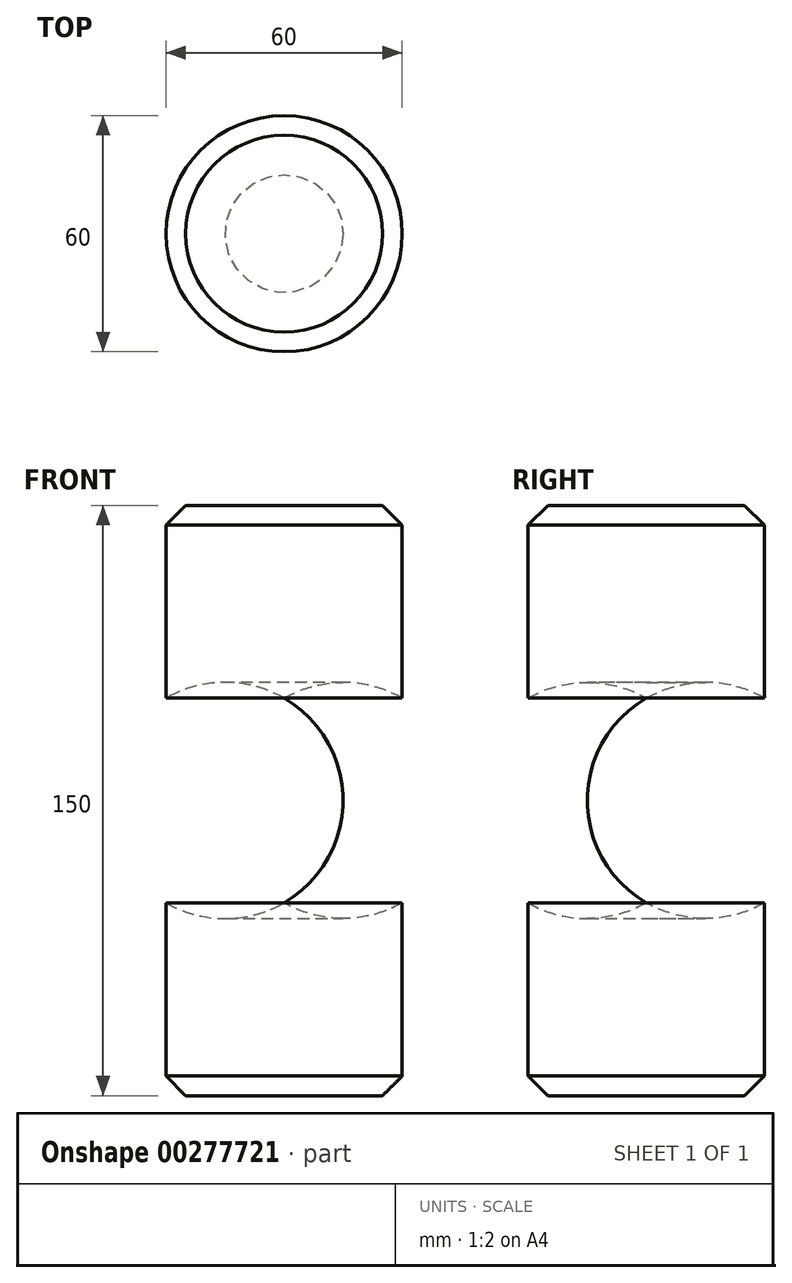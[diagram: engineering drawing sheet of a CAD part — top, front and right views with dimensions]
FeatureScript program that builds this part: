
annotation { "Feature Type Name" : "Feature", "Feature Type Description" : "" }
export const myFeature = defineFeature(function(context is Context, id is Id, definition is map)
    precondition{}
    {
        {
            var Q0;
            Q0=qCreatedBy(makeId("Front.planeOp"),FACE);
            var sketch = newSketch(context, id + "F0", { "sketchPlane" : qUnion([Q0])});
            skLineSegment(sketch, "E0", {"start": v(0, 75) * mm, "end": v(30, 75) * mm});
            skLineSegment(sketch, "E1", {"start": v(30, 75) * mm, "end": v(30, 25.98) * mm});
            skArc(sketch, "E2", {"start": v(30, -25.98) * mm, "mid": v(45, 0) * mm, "end": v(30, 25.98) * mm});
            skLineSegment(sketch, "E3", {"start": v(30, -25.98) * mm, "end": v(30, -75) * mm});
            skLineSegment(sketch, "E4", {"start": v(30, -75) * mm, "end": v(0, -75) * mm});
            skLineSegment(sketch, "E5", {"start": v(0, -75) * mm, "end": v(0, 75) * mm});
            skSolve(sketch);
        }
        {
            var Q0;
            Q0=makeQuery(id+"F0.imprint","IMPRINT",FACE,{"disambiguationData":[TD([[makeQuery(id+"F0.imprint","IMPRINT",EDGE,{"derivedFrom":sQuery(id+"F0.wireOp",EDGE,"E0")}),-1.0]])]});
            var Q1;
            Q1=sQuery(id+"F0.wireOp",EDGE,"E5");
            revolve(context, id + "F1", {"entities" : qUnion([Q0]), "axis" : qUnion([Q1]), "revolveType" : RevolveType.FULL});
        }
        {
            var Q0;
            Q0=qCreatedBy(makeId("Right.planeOp"),FACE);
            cPlane(context, id + "F2", {"entities" : qUnion([Q0]), "cplaneType" : CPlaneType.OFFSET, "offset" : 30 * mm, "width" : 150 * mm, "height" : 150 * mm});
        }
        {
            var Q0;
            Q0=qCreatedBy(id+"F2.planeOp",FACE);
            var sketch = newSketch(context, id + "F3", { "sketchPlane" : qUnion([Q0])});
            skEllipse(sketch, "E6", {"center": v(0, 0) * mm, "majorRadius": 20 * mm, "minorRadius": 10 * mm, "majorAxis": v(0, 1)});
            skSolve(sketch);
        }
        {
            var Q0;
            Q0=qCreatedBy(makeId("Front.planeOp"),FACE);
            var sketch = newSketch(context, id + "F4", { "sketchPlane" : qUnion([Q0])});
            skFitSpline(sketch, "E7", {"points": [v(30.54, 0) * mm, v(121.7, 9.88) * mm, v(170.2, 75) * mm, v(260.02, 115.86) * mm], "startDerivative": vector(310.56, -24.64) * mm, "endDerivative": vector(294.86, 80.72) * mm});
            skSolve(sketch);
        }
        {
            var Q0;
            Q0 = qSketchRegion(id + "F3", true);
            var Q1;
            Q1 = qConstructionFilter(qBodyType(qCreatedBy(id + "F4" ,EDGE), BodyType.WIRE), ConstructionObject.NO);
            sweep(context, id + "F5", {"operationType" : NewBodyOperationType.ADD, "profiles" : qUnion([Q0]), "path" : qUnion([Q1])});
        }
        {
            var Q0;
            Q0=makeQuery(id+"F1.opRevolve","SWEPT_BODY",BODY,{"disambiguationData":[OSD([sQuery(id+"F0.wireOp",EDGE,"E0"),sQuery(id+"F0.wireOp",EDGE,"E1"),sQuery(id+"F0.wireOp",EDGE,"E2"),sQuery(id+"F0.wireOp",EDGE,"E3"),sQuery(id+"F0.wireOp",EDGE,"E4"),sQuery(id+"F0.wireOp",EDGE,"E5")])]});
            var Q1;
            Q1=makeQuery(id+"F1.opRevolve","SWEPT_FACE",FACE,{"disambiguationData":[OSD([sQuery(id+"F0.wireOp",EDGE,"E1")])]});
            circularPattern(context, id + "F6", {"entities" : qUnion([Q0]), "axis" : qUnion([Q1]), "angle" : 360 * degree, "instanceCount" : 5, "equalSpace" : true});
        }
        {
            var Q0;
            Q0=qCreatedBy(makeId("Front.planeOp"),FACE);
            var sketch = newSketch(context, id + "F7", { "sketchPlane" : qUnion([Q0])});
            skCircle(sketch, "E8", {"center": v(280, 120) * mm, "radius": 30 * mm});
            skSolve(sketch);
        }
        {
            var Q0;
            Q0=makeQuery(id+"F7.imprint","IMPRINT",FACE,{"disambiguationData":[TD([[makeQuery(id+"F7.imprint","IMPRINT",EDGE,{"derivedFrom":sQuery(id+"F7.wireOp",EDGE,"E8")}),1.0]])]});
            var Q1;
            Q1=makeQuery(id+"F1.opRevolve","SWEPT_FACE",FACE,{"disambiguationData":[OSD([sQuery(id+"F0.wireOp",EDGE,"E1")])]});
            revolve(context, id + "F8", {"operationType" : NewBodyOperationType.ADD, "entities" : qUnion([Q0]), "axis" : qUnion([Q1]), "revolveType" : RevolveType.FULL});
        }
        {
            var Q0;
            Q0=makeQuery(id+"F5.boolean.opBoolean","INTERSECT",EDGE,{"derivedFrom":[makeQuery(id+"F1.opRevolve","SWEPT_FACE",FACE,{"disambiguationData":[OSD([sQuery(id+"F0.wireOp",EDGE,"E2")])]}),makeQuery(id+"F5.opSweep","SWEPT_FACE",FACE,{"disambiguationData":[OSD([sQuery(id+"F3.wireOp",EDGE,"E6"),sQuery(id+"F4.wireOp",EDGE,"E7")])]})]});
            var Q1;
            {var subQ0=makeQuery(id+"F1.opRevolve","SWEPT_FACE",FACE,{"disambiguationData":[OSD([sQuery(id+"F0.wireOp",EDGE,"E2")])]});Q1=makeQuery(id+"F8.boolean.opBoolean","INTERSECT",EDGE,{"derivedFrom":[subQ0,makeQuery(id+"F6.opPattern","COPY",FACE,{"derivedFrom":subQ0,"instanceName":"1"}),makeQuery(id+"F6.opPattern","COPY",FACE,{"derivedFrom":subQ0,"instanceName":"2"}),makeQuery(id+"F6.opPattern","COPY",FACE,{"derivedFrom":subQ0,"instanceName":"3"})]});}
            var Q2;
            {var subQ0=makeQuery(id+"F1.opRevolve","SWEPT_FACE",FACE,{"disambiguationData":[OSD([sQuery(id+"F0.wireOp",EDGE,"E2")])]});Q2=makeQuery(id+"F8.boolean.opBoolean","INTERSECT",EDGE,{"derivedFrom":[subQ0,makeQuery(id+"F6.opPattern","COPY",FACE,{"derivedFrom":subQ0,"instanceName":"1"}),makeQuery(id+"F6.opPattern","COPY",FACE,{"derivedFrom":subQ0,"instanceName":"2"}),makeQuery(id+"F6.opPattern","COPY",FACE,{"derivedFrom":subQ0,"instanceName":"4"})]});}
            var Q3;
            {var subQ0=makeQuery(id+"F1.opRevolve","SWEPT_FACE",FACE,{"disambiguationData":[OSD([sQuery(id+"F0.wireOp",EDGE,"E2")])]});Q3=makeQuery(id+"F8.boolean.opBoolean","INTERSECT",EDGE,{"derivedFrom":[subQ0,makeQuery(id+"F6.opPattern","COPY",FACE,{"derivedFrom":subQ0,"instanceName":"1"}),makeQuery(id+"F6.opPattern","COPY",FACE,{"derivedFrom":subQ0,"instanceName":"3"})]});}
            var Q4;
            {var subQ0=makeQuery(id+"F1.opRevolve","SWEPT_FACE",FACE,{"disambiguationData":[OSD([sQuery(id+"F0.wireOp",EDGE,"E2")])]});Q4=makeQuery(id+"F8.boolean.opBoolean","INTERSECT",EDGE,{"derivedFrom":[subQ0,makeQuery(id+"F6.opPattern","COPY",FACE,{"derivedFrom":subQ0,"instanceName":"2"})]});}
            fillet(context, id + "F9", {"entities" : qUnion([Q0, Q1, Q2, Q3, Q4]), "radius" : 10 * mm, "tangentPropagation" : true, "allowEdgeOverflow" : false});
        }
        {
            var Q0;
            Q0=makeQuery(id+"F8.boolean.opBoolean","INTERSECT",EDGE,{"derivedFrom":[makeQuery(id+"F5.opSweep","SWEPT_FACE",FACE,{"disambiguationData":[OSD([sQuery(id+"F3.wireOp",EDGE,"E6"),sQuery(id+"F4.wireOp",EDGE,"E7")])]}),makeQuery(id+"F8.opRevolve","SWEPT_FACE",FACE,{"disambiguationData":[OSD([sQuery(id+"F7.wireOp",EDGE,"E8")])]})]});
            var Q1;
            Q1=makeQuery(id+"F8.boolean.opBoolean","INTERSECT",EDGE,{"derivedFrom":[makeQuery(id+"F6.opPattern","COPY",FACE,{"derivedFrom":makeQuery(id+"F5.opSweep","SWEPT_FACE",FACE,{"disambiguationData":[OSD([sQuery(id+"F3.wireOp",EDGE,"E6"),sQuery(id+"F4.wireOp",EDGE,"E7")])]}),"instanceName":"1"}),makeQuery(id+"F8.opRevolve","SWEPT_FACE",FACE,{"disambiguationData":[OSD([sQuery(id+"F7.wireOp",EDGE,"E8")])]})]});
            var Q2;
            Q2=makeQuery(id+"F8.boolean.opBoolean","INTERSECT",EDGE,{"derivedFrom":[makeQuery(id+"F6.opPattern","COPY",FACE,{"derivedFrom":makeQuery(id+"F5.opSweep","SWEPT_FACE",FACE,{"disambiguationData":[OSD([sQuery(id+"F3.wireOp",EDGE,"E6"),sQuery(id+"F4.wireOp",EDGE,"E7")])]}),"instanceName":"2"}),makeQuery(id+"F8.opRevolve","SWEPT_FACE",FACE,{"disambiguationData":[OSD([sQuery(id+"F7.wireOp",EDGE,"E8")])]})]});
            var Q3;
            Q3=makeQuery(id+"F8.boolean.opBoolean","INTERSECT",EDGE,{"derivedFrom":[makeQuery(id+"F6.opPattern","COPY",FACE,{"derivedFrom":makeQuery(id+"F5.opSweep","SWEPT_FACE",FACE,{"disambiguationData":[OSD([sQuery(id+"F3.wireOp",EDGE,"E6"),sQuery(id+"F4.wireOp",EDGE,"E7")])]}),"instanceName":"3"}),makeQuery(id+"F8.opRevolve","SWEPT_FACE",FACE,{"disambiguationData":[OSD([sQuery(id+"F7.wireOp",EDGE,"E8")])]})]});
            var Q4;
            Q4=makeQuery(id+"F8.boolean.opBoolean","INTERSECT",EDGE,{"derivedFrom":[makeQuery(id+"F6.opPattern","COPY",FACE,{"derivedFrom":makeQuery(id+"F5.opSweep","SWEPT_FACE",FACE,{"disambiguationData":[OSD([sQuery(id+"F3.wireOp",EDGE,"E6"),sQuery(id+"F4.wireOp",EDGE,"E7")])]}),"instanceName":"4"}),makeQuery(id+"F8.opRevolve","SWEPT_FACE",FACE,{"disambiguationData":[OSD([sQuery(id+"F7.wireOp",EDGE,"E8")])]})]});
            fillet(context, id + "F10", {"entities" : qUnion([Q0, Q1, Q2, Q3, Q4]), "radius" : 3 * mm, "tangentPropagation" : true, "allowEdgeOverflow" : false});
        }
        {
            var Q0;
            Q0=makeQuery(id+"F1.opRevolve","SWEPT_EDGE",EDGE,{"disambiguationData":[OSD([sQuery(id+"F0.wireOp",EDGE,"E0"),sQuery(id+"F0.wireOp",EDGE,"E1")])]});
            var Q1;
            Q1=makeQuery(id+"F1.opRevolve","SWEPT_FACE",FACE,{"disambiguationData":[OSD([sQuery(id+"F0.wireOp",EDGE,"E4")])]});
            chamfer(context, id + "F11", {"entities" : qUnion([Q0, Q1]), "width" : 5 * mm, "tangentPropagation" : true});
        }
    });
